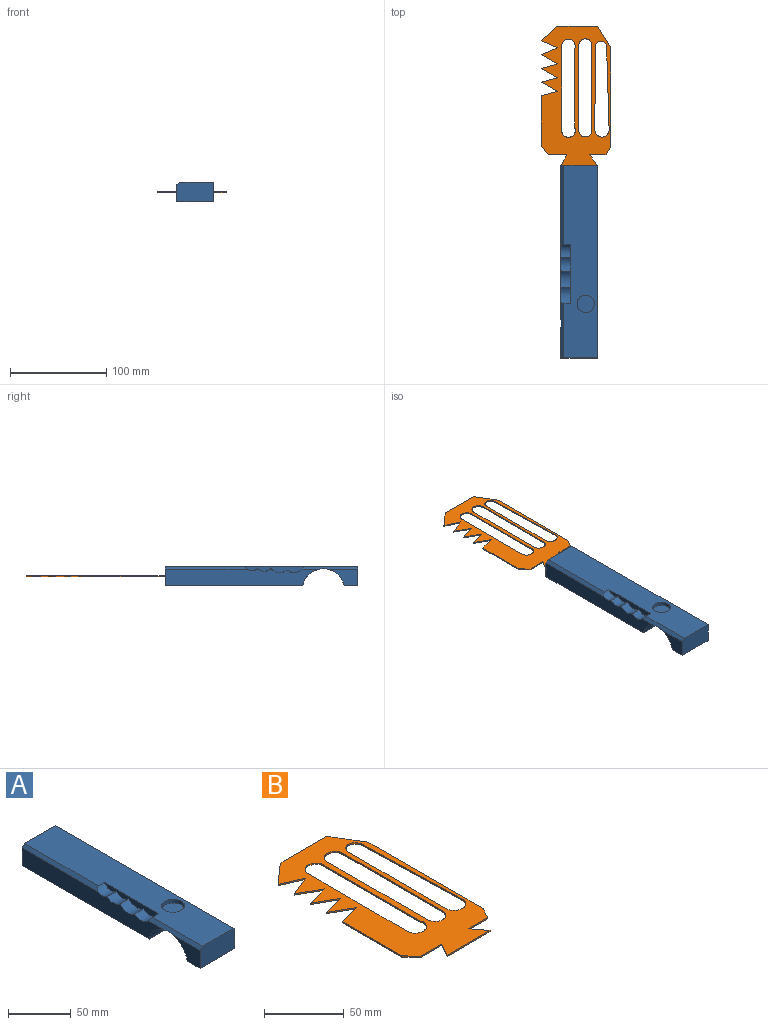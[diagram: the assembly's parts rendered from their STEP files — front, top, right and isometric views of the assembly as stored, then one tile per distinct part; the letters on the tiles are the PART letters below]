
ASSEMBLY  parts=2 mates=1
PART A: 20 faces, bbox 38x200x20 mm
  f0: plane 159.86x17.22mm, normal (-1,0,0), area 2426.9mm2, adj f3,f5,f6,f7,f8,f9,f10,f16
  f1: plane 31.56x17.22mm, normal (-1,0,0), area 335.5mm2, adj f4,f5,f11,f19
  f2: plane 200x34.87mm, normal (0,0,1), area 6295.3mm2, adj f3,f4,f6,f7,f12,f13,f14,f18
  f3: plane 38x20mm, normal (0,1,0), area 755.7mm2, adj f0,f2,f10,f12,f18
  f4: plane 38x20mm, normal (0,-1,0), area 755.7mm2, adj f1,f2,f11,f12,f19
  f5: cylinder r=21.79mm len=42.79mm, axis (-1,0,0), area 2282.2mm2, adj f0,f1,f10,f11,f12,f19
  f6: cylinder r=10.74mm len=17.06mm, axis (-1,0,0), area 199.4mm2, adj f0,f2,f8,f13,f19
  f7: cylinder r=9.07mm len=13.4mm, axis (-1,0,0), area 148.2mm2, adj f0,f2,f9,f13,f16,f18
  f8: cylinder r=12.24mm len=16.63mm, axis (-1,0,0), area 183.6mm2, adj f0,f6,f9,f13,f17
  f9: cylinder r=10.54mm len=14.11mm, axis (-1,0,0), area 154.3mm2, adj f0,f7,f8,f13,f16,f17
  f10: plane 142.75x38mm, normal (0,0,-1), area 5424.5mm2, adj f0,f3,f5,f12
  f11: plane 38x14.46mm, normal (0,0,-1), area 549.4mm2, adj f1,f4,f5,f12
  f12: plane 200x20mm, normal (1,0,0), area 3433.4mm2, adj f2,f3,f4,f5,f10,f11
  f13: plane 61.21x6.58mm, normal (-1,0,0), area 282.7mm2, adj f2,f6,f7,f8,f9
  f14: cylinder r=9.06mm len=18.13mm, axis (0,0,1), area 215.8mm2, adj f2,f15
  f15: plane 18.13x18.13mm, normal (0,0,1), area 258.1mm2, adj f14
  f16: plane 0.97x0.44mm, normal (-0.66,0,0.75), area 0.3mm2, adj f0,f7,f9
  f17: plane 0.82x0.44mm, normal (-0.66,0,0.75), area 0.2mm2, adj f0,f8,f9
  f18: plane 84.98x3.13mm, normal (-0.66,0,0.75), area 349.3mm2, adj f0,f2,f3,f7
  f19: plane 58.14x3.13mm, normal (-0.66,0,0.75), area 235.6mm2, adj f0,f1,f2,f4,f5,f6
PART B: 34 faces, bbox 72.3x144.6x1 mm
  f0: plane 144.64x72.27mm, normal (0,0,1), area 5191.7mm2, adj f2,f3,f4,f5,f6,f7,f8,f9
  f1: plane 144.64x72.27mm, normal (0,0,-1), area 5191.7mm2, adj f2,f3,f4,f5,f6,f7,f8,f9
  f2: plane 8.78x4.98mm, normal (0.87,-0.49,0), area 10.1mm2, adj f0,f1,f3,f21
  f3: plane 102.2x1mm, normal (1,0,0), area 102.2mm2, adj f0,f1,f2,f4
  f4: plane 22.72x13.76mm, normal (0.86,0.52,0), area 26.6mm2, adj f0,f1,f3,f5
  f5: plane 41.27x1mm, normal (0,1,0), area 41.3mm2, adj f0,f1,f4,f6
  f6: plane 17.25x15.22mm, normal (-0.66,0.75,0), area 23mm2, adj f0,f1,f5,f7
  f7: plane 17.02x7.5mm, normal (-0.4,-0.91,0), area 18.6mm2, adj f0,f1,f6,f8
  f8: plane 17.02x6.98mm, normal (-0.38,0.93,0), area 18.4mm2, adj f0,f1,f7,f9
  f9: plane 17.02x9.65mm, normal (-0.49,-0.87,0), area 19.6mm2, adj f0,f1,f8,f10
  f10: plane 17.02x4.83mm, normal (-0.27,0.96,0), area 17.7mm2, adj f0,f1,f9,f11
  f11: plane 17.02x9.65mm, normal (-0.49,-0.87,0), area 19.6mm2, adj f0,f1,f10,f12
  f12: plane 17.02x4.39mm, normal (-0.25,0.97,0), area 17.6mm2, adj f0,f1,f11,f13
  f13: plane 17.02x9.65mm, normal (-0.49,-0.87,0), area 19.6mm2, adj f0,f1,f12,f14
  f14: plane 17.02x4.44mm, normal (-0.25,0.97,0), area 17.6mm2, adj f0,f1,f13,f15
  f15: plane 52.6x1mm, normal (-1,0,0), area 52.6mm2, adj f0,f1,f14,f16
  f16: plane 8.78x7.8mm, normal (-0.75,-0.66,0), area 11.7mm2, adj f0,f1,f15,f17
  f17: plane 18.92x1mm, normal (0,-1,0), area 18.9mm2, adj f0,f1,f16,f18
  f18: plane 10.94x6.21mm, normal (-0.87,0.49,0), area 12.6mm2, adj f0,f1,f17,f19
  f19: plane 38x1mm, normal (0,-1,0), area 38mm2, adj f0,f1,f18,f20
  f20: plane 10.94x8.15mm, normal (0.8,0.6,0), area 13.6mm2, adj f0,f1,f19,f21
  f21: plane 16.93x1mm, normal (0,-1,0), area 16.9mm2, adj f0,f1,f2,f20
  f22: plane 89.33x1mm, normal (-1,0,0), area 89.3mm2, adj f0,f1,f23,f25
  f23: cylinder r=6.78mm len=13.55mm, axis (0,0,1), area 21.3mm2, adj f0,f1,f22,f24
  f24: plane 89.33x1mm, normal (1,0,0), area 89.3mm2, adj f0,f1,f23,f25
  f25: cylinder r=6.86mm len=13.55mm, axis (0,0,1), area 19.4mm2, adj f0,f1,f22,f24
  f26: plane 85.09x2.57mm, normal (-1,-0.03,0), area 85.1mm2, adj f0,f1,f27,f29
  f27: cylinder r=5.97mm len=11.95mm, axis (0,0,1), area 19.7mm2, adj f0,f1,f26,f28
  f28: plane 86.18x1mm, normal (1,0,0), area 86.2mm2, adj f0,f1,f27,f29
  f29: cylinder r=7.37mm len=14.73mm, axis (0,0,1), area 23.4mm2, adj f0,f1,f26,f28
  f30: cylinder r=7.03mm len=14.05mm, axis (0,0,1), area 26.1mm2, adj f0,f1,f31,f33
  f31: plane 86.16x1mm, normal (1,0,0), area 86.2mm2, adj f0,f1,f30,f32
  f32: cylinder r=7.09mm len=14.18mm, axis (0,0,1), area 24.9mm2, adj f0,f1,f31,f33
  f33: plane 82.74x1mm, normal (-1,0,0), area 82.7mm2, adj f0,f1,f30,f32
PLACE A t=(59,-173.66,26.11)mm
PLACE B t=(84.45,22.87,-10.65)mm
MATE fastened A.f3 <-> B.f19  axis (0,1,0) through (78.1,-35.95,-10.15)mm
